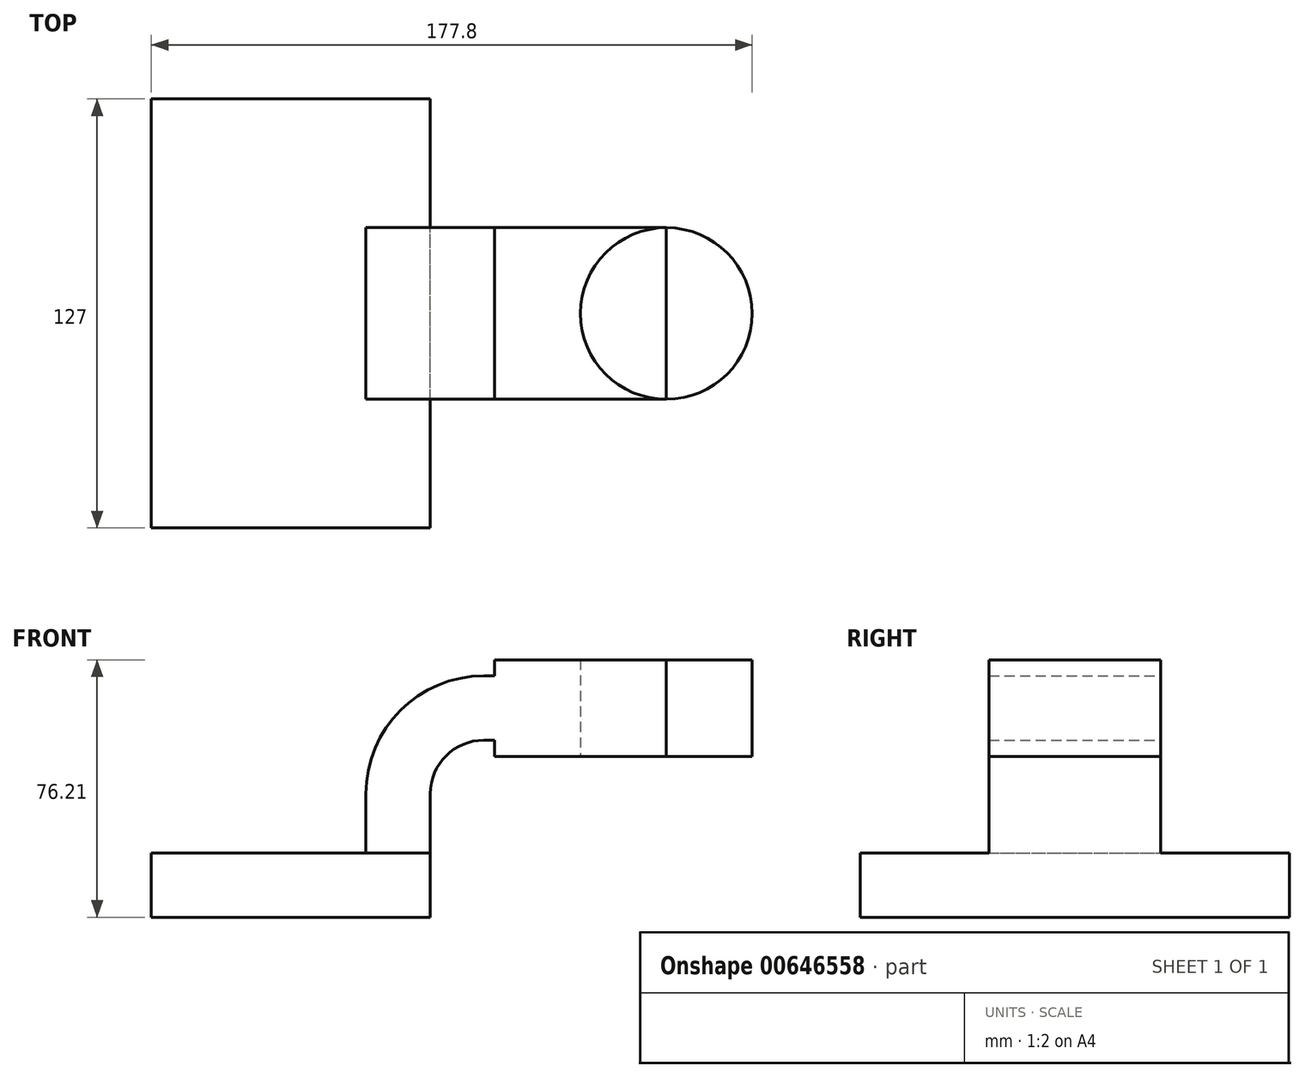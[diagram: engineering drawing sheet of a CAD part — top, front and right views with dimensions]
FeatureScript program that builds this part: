
annotation { "Feature Type Name" : "Feature", "Feature Type Description" : "" }
export const myFeature = defineFeature(function(context is Context, id is Id, definition is map)
    precondition{}
    {
        {
            var Q0;
            Q0=qCreatedBy(makeId("Front.planeOp"),FACE);
            var sketch = newSketch(context, id + "F0", { "sketchPlane" : qUnion([Q0])});
            skLineSegment(sketch, "E0.bottom", {"start": v(-41.28, -9.53) * mm, "end": v(41.28, -9.53) * mm});
            skLineSegment(sketch, "E0.top", {"start": v(-41.28, 9.53) * mm, "end": v(41.28, 9.53) * mm});
            skLineSegment(sketch, "E0.left", {"start": v(-41.28, -9.53) * mm, "end": v(-41.28, 9.52) * mm});
            skLineSegment(sketch, "E0.right", {"start": v(41.28, -9.53) * mm, "end": v(41.28, 9.52) * mm});
            skPoint(sketch, "E0.middle", {"position": v(0, 0) * mm});
            skLineSegment(sketch, "E1.bottom", {"start": v(60.33, 38.1) * mm, "end": v(111.12, 38.1) * mm});
            skLineSegment(sketch, "E1.top", {"start": v(60.32, 66.67) * mm, "end": v(111.12, 66.67) * mm});
            skLineSegment(sketch, "E1.left", {"start": v(60.32, 38.1) * mm, "end": v(60.32, 66.67) * mm});
            skLineSegment(sketch, "E1.right", {"start": v(111.12, 38.1) * mm, "end": v(111.12, 66.67) * mm});
            skPoint(sketch, "E1.middle", {"position": v(85.72, 52.39) * mm});
            skLineSegment(sketch, "E2", {"start": v(41.27, 9.52) * mm, "end": v(41.27, 27) * mm});
            skArc(sketch, "E3", {"start": v(41.28, 27) * mm, "mid": v(45.92, 38.23) * mm, "end": v(57.15, 42.88) * mm});
            skPoint(sketch, "E4.end.orphan", {"position": v(82.16, 27) * mm});
            skLineSegment(sketch, "E5", {"start": v(57.15, 42.88) * mm, "end": v(81.68, 42.88) * mm});
            skLineSegment(sketch, "E6.0", {"start": v(57.15, 61.93) * mm, "end": v(81.68, 61.93) * mm});
            skArc(sketch, "E6.1", {"start": v(22.23, 27) * mm, "mid": v(32.45, 51.7) * mm, "end": v(57.15, 61.93) * mm});
            skLineSegment(sketch, "E6.2", {"start": v(22.23, 9.52) * mm, "end": v(22.23, 27) * mm});
            skLineSegment(sketch, "E7", {"start": v(81.68, 61.93) * mm, "end": v(81.68, 42.88) * mm});
            skFitSpline(sketch, "E8", {"points": [v(-41.28, 9.53) * mm, v(57.15, 61.93) * mm], "startDerivative": vector(98.43, 52.4) * mm, "endDerivative": vector(128.35, -37.58) * mm});
            skLineSegment(sketch, "E9", {"start": v(85.72, 66.67) * mm, "end": v(85.72, 38.1) * mm});
            skSolve(sketch);
        }
        {
            var Q0;
            Q0=makeQuery(id+"F0.imprint","IMPRINT",FACE,{"disambiguationData":[TD([[makeQuery(id+"F0.imprint","IMPRINT",EDGE,{"derivedFrom":sQuery(id+"F0.wireOp",EDGE,"E0.bottom")}),1.0]])]});
            extrude(context, id + "F1", {"entities" : qUnion([Q0]), "depth" : 127 * mm, "offsetDistance" : 25.4 * mm, "symmetric" : true});
        }
        {
            var Q0;
            {var subQ4=sQuery(id+"F0.wireOp",EDGE,"E1.bottom");Q0=makeQuery(id+"F0.imprint","IMPRINT",FACE,{"disambiguationData":[TD([[makeQuery(id+"F0.imprint","IMPRINT",EDGE,{"derivedFrom":subQ4}),1.0]])]});}
            var Q1;
            {var subQ5=sQuery(id+"F0.wireOp",EDGE,"E7");Q1=makeQuery(id+"F0.imprint","IMPRINT",FACE,{"disambiguationData":[TD([[makeQuery(id+"F0.imprint","IMPRINT",EDGE,{"derivedFrom":subQ5}),-1.0]])]});}
            var Q2;
            {var subQ0=sQuery(id+"F0.wireOp",EDGE,"E2");Q2=makeQuery(id+"F0.imprint","IMPRINT",FACE,{"disambiguationData":[TD([[makeQuery(id+"F0.imprint","IMPRINT",EDGE,{"derivedFrom":subQ0}),1.0]])]});}
            var Q3;
            {var subQ10=sQuery(id+"F0.wireOp",EDGE,"E7");Q3=makeQuery(id+"F0.imprint","IMPRINT",FACE,{"disambiguationData":[TD([[makeQuery(id+"F0.imprint","IMPRINT",EDGE,{"derivedFrom":subQ10}),1.0]])]});}
            extrude(context, id + "F2", {"entities" : qUnion([Q0, Q1, Q2, Q3]), "operationType" : NewBodyOperationType.ADD, "depth" : 50.8 * mm, "offsetDistance" : 25.4 * mm, "symmetric" : true});
        }
        {
            var Q0;
            Q0=makeQuery(id+"F0.imprint","IMPRINT",FACE,{"disambiguationData":[TD([[makeQuery(id+"F0.imprint","IMPRINT",EDGE,{"derivedFrom":sQuery(id+"F0.wireOp",EDGE,"E6.1")}),1.0]])]});
            extrude(context, id + "F3", {"entities" : qUnion([Q0]), "operationType" : NewBodyOperationType.ADD, "depth" : 15.88 * mm, "offsetDistance" : 25.4 * mm, "symmetric" : true});
        }
        {
            var Q0;
            {var subQ0=sQuery(id+"F0.wireOp",EDGE,"E1.right");Q0=makeQuery(id+"F0.imprint","IMPRINT",FACE,{"disambiguationData":[TD([[makeQuery(id+"F0.imprint","IMPRINT",EDGE,{"derivedFrom":subQ0}),1.0]])]});}
            var Q1;
            Q1=sQuery(id+"F0.wireOp",EDGE,"E1.right");
            revolve(context, id + "F4", {"entities" : qUnion([Q0]), "axis" : qUnion([Q1]), "revolveType" : RevolveType.FULL});
        }
    });
